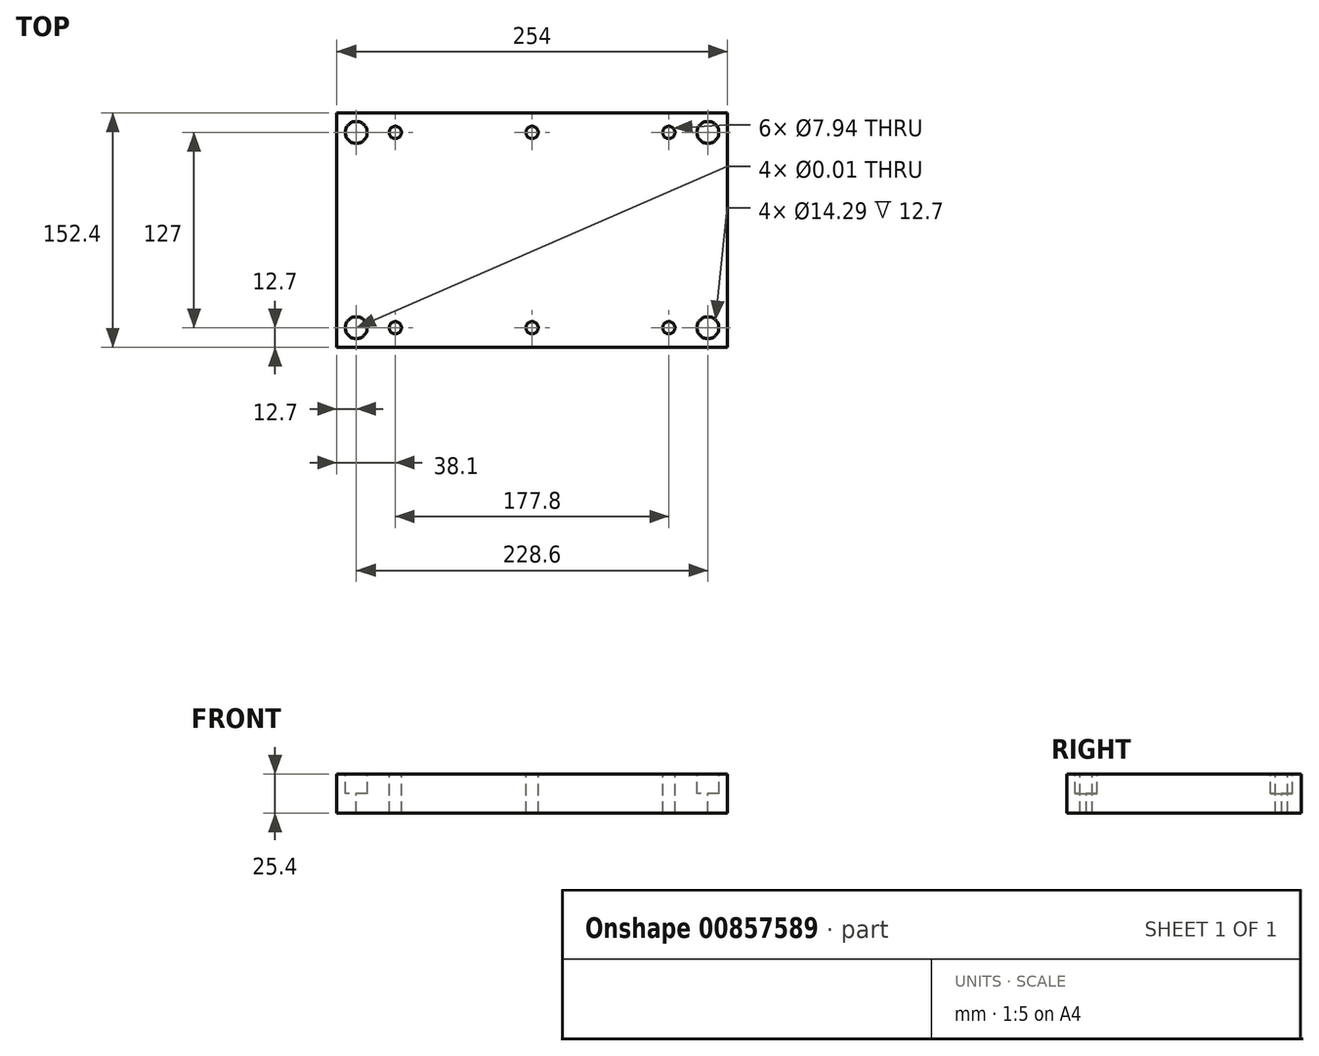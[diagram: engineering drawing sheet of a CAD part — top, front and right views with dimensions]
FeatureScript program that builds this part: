
annotation { "Feature Type Name" : "Feature", "Feature Type Description" : "" }
export const myFeature = defineFeature(function(context is Context, id is Id, definition is map)
    precondition{}
    {
        {
            var Q0;
            Q0=qCreatedBy(makeId("Top.planeOp"),FACE);
            var sketch = newSketch(context, id + "F0", { "sketchPlane" : qUnion([Q0])});
            skLineSegment(sketch, "E0.bottom", {"start": v(127, 76.2) * mm, "end": v(-127, 76.2) * mm});
            skLineSegment(sketch, "E0.top", {"start": v(127, -76.2) * mm, "end": v(-127, -76.2) * mm});
            skLineSegment(sketch, "E0.left", {"start": v(127, 76.2) * mm, "end": v(127, -76.2) * mm});
            skLineSegment(sketch, "E0.right", {"start": v(-127, 76.2) * mm, "end": v(-127, -76.2) * mm});
            skPoint(sketch, "E0.middle", {"position": v(0, 0) * mm});
            skSolve(sketch);
        }
        {
            var Q0;
            Q0=makeQuery(id+"F0.imprint","IMPRINT",FACE,{"disambiguationData":[TD([[makeQuery(id+"F0.imprint","IMPRINT",EDGE,{"derivedFrom":sQuery(id+"F0.wireOp",EDGE,"E0.bottom")}),1.0]])]});
            extrude(context, id + "F1", {"entities" : qUnion([Q0]), "depth" : 25.4 * mm, "offsetDistance" : 25.4 * mm});
        }
        {
            var Q0;
            Q0=makeQuery(id+"F1.opExtrude","CAP_FACE",FACE,{"disambiguationData":[OSD([sQuery(id+"F0.wireOp",EDGE,"E0.bottom"),sQuery(id+"F0.wireOp",EDGE,"E0.top"),sQuery(id+"F0.wireOp",EDGE,"E0.left"),sQuery(id+"F0.wireOp",EDGE,"E0.right")])],"isStart":false});
            var sketch = newSketch(context, id + "F2", { "sketchPlane" : qUnion([Q0])});
            skPoint(sketch, "E1", {"position": v(-114.3, 63.5) * mm});
            skPoint(sketch, "E2", {"position": v(-114.3, -63.5) * mm});
            skPoint(sketch, "E3", {"position": v(114.3, 63.5) * mm});
            skPoint(sketch, "E4", {"position": v(114.3, -63.5) * mm});
            skSolve(sketch);
        }
        {
            var Q0;
            Q0=sQuery(id+"F2.wireOp",VERTEX,"E1");
            var Q1;
            Q1=sQuery(id+"F2.wireOp",VERTEX,"E2");
            var Q2;
            Q2=sQuery(id+"F2.wireOp",VERTEX,"E3");
            var Q3;
            Q3=sQuery(id+"F2.wireOp",VERTEX,"E4");
            var Q4;
            Q4=makeQuery(id+"F1.opExtrude","SWEPT_BODY",BODY,{"disambiguationData":[OSD([sQuery(id+"F0.wireOp",EDGE,"E0.bottom"),sQuery(id+"F0.wireOp",EDGE,"E0.top"),sQuery(id+"F0.wireOp",EDGE,"E0.left"),sQuery(id+"F0.wireOp",EDGE,"E0.right")])]});
            hole(context, id + "F3", {"style" : HoleStyle.C_BORE, "endStyle" : HoleEndStyle.THROUGH, "standardTappedOrClearance" : lookupTablePath({ "standard" : "ANSI", "size" : "3/8 (0.38)", "type" : "Drilled" }), "standardBlindInLast" : lookupTablePath({ "standard" : "ANSI", "size" : "3/8", "type" : "Drilled" }), "holeDiameter" : 3 / 203.2 * mm, "cBoreDiameter" : 14.29 * mm, "cBoreDepth" : 12.7 * mm, "majorDiameter" : 19.05 * mm, "isTappedThrough" : true, "tappedDepth" : 30.48 * mm, "tapClearance" : 3, "locations" : qUnion([Q0, Q1, Q2, Q3]), "scope" : qUnion([Q4])});
        }
        {
            var Q0;
            Q0=makeQuery(id+"F1.opExtrude","CAP_FACE",FACE,{"disambiguationData":[OSD([sQuery(id+"F0.wireOp",EDGE,"E0.bottom"),sQuery(id+"F0.wireOp",EDGE,"E0.top"),sQuery(id+"F0.wireOp",EDGE,"E0.left"),sQuery(id+"F0.wireOp",EDGE,"E0.right")])],"isStart":false});
            var sketch = newSketch(context, id + "F4", { "sketchPlane" : qUnion([Q0])});
            skPoint(sketch, "E5", {"position": v(0, 63.5) * mm});
            skPoint(sketch, "E5.positionSnap0", {"position": v(0, 76.2) * mm});
            skPoint(sketch, "E6", {"position": v(-88.9, 63.5) * mm});
            skPoint(sketch, "E7", {"position": v(88.9, 63.5) * mm});
            skPoint(sketch, "E8", {"position": v(0, -63.5) * mm});
            skPoint(sketch, "E8.positionSnap0", {"position": v(0, -76.2) * mm});
            skPoint(sketch, "E9", {"position": v(-88.9, -63.5) * mm});
            skPoint(sketch, "E10", {"position": v(88.9, -63.5) * mm});
            skSolve(sketch);
        }
        {
            var Q0;
            Q0=sQuery(id+"F4.wireOp",VERTEX,"E6");
            var Q1;
            Q1=sQuery(id+"F4.wireOp",VERTEX,"E5");
            var Q2;
            Q2=sQuery(id+"F4.wireOp",VERTEX,"E7");
            var Q3;
            Q3=sQuery(id+"F4.wireOp",VERTEX,"E10");
            var Q4;
            Q4=sQuery(id+"F4.wireOp",VERTEX,"E8");
            var Q5;
            Q5=sQuery(id+"F4.wireOp",VERTEX,"E9");
            var Q6;
            Q6=makeQuery(id+"F1.opExtrude","SWEPT_BODY",BODY,{"disambiguationData":[OSD([sQuery(id+"F0.wireOp",EDGE,"E0.bottom"),sQuery(id+"F0.wireOp",EDGE,"E0.top"),sQuery(id+"F0.wireOp",EDGE,"E0.left"),sQuery(id+"F0.wireOp",EDGE,"E0.right")])]});
            hole(context, id + "F5", {"style" : HoleStyle.SIMPLE, "endStyle" : HoleEndStyle.THROUGH, "standardTappedOrClearance" : lookupTablePath({ "standard" : "ANSI", "engagement" : "75%", "pitch" : "16 tpi", "size" : "3/8", "type" : "Tapped" }), "standardBlindInLast" : lookupTablePath({ "standard" : "ANSI", "engagement" : "75%", "pitch" : "16 tpi", "size" : "3/8", "type" : "Tapped" }), "holeDiameter" : 7.94 * mm, "majorDiameter" : 9.52 * mm, "showTappedDepth" : true, "isTappedThrough" : true, "tappedDepth" : 30.48 * mm, "tapClearance" : 3, "locations" : qUnion([Q0, Q1, Q2, Q3, Q4, Q5]), "scope" : qUnion([Q6])});
        }
    });
